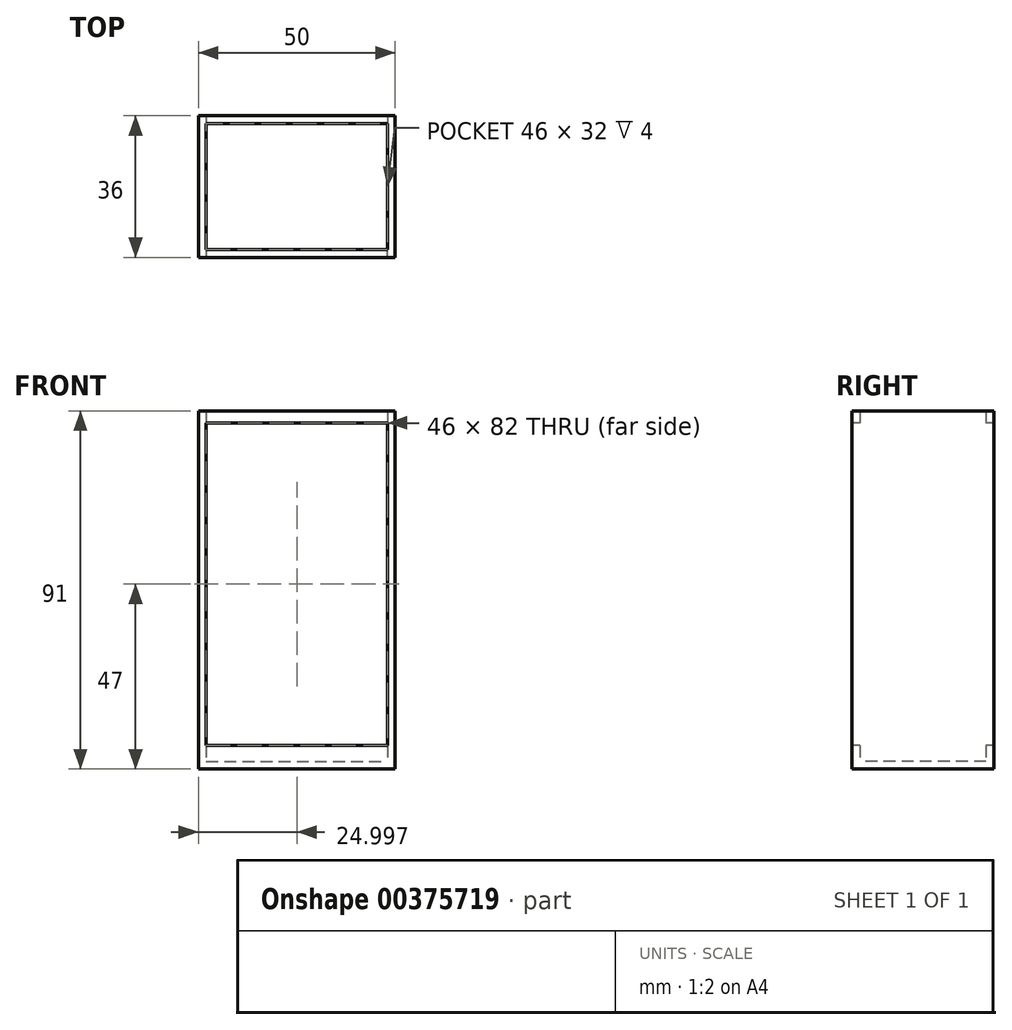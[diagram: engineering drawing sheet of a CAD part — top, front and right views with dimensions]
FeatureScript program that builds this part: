
annotation { "Feature Type Name" : "Feature", "Feature Type Description" : "" }
export const myFeature = defineFeature(function(context is Context, id is Id, definition is map)
    precondition{}
    {
        {
            var Q0;
            Q0=qCreatedBy(makeId("Top.planeOp"),FACE);
            var sketch = newSketch(context, id + "F0", { "sketchPlane" : qUnion([Q0])});
            skLineSegment(sketch, "E0.bottom", {"start": v(-57.9, 42.38) * mm, "end": v(-7.9, 42.38) * mm});
            skLineSegment(sketch, "E0.top", {"start": v(-57.9, 6.38) * mm, "end": v(-7.9, 6.38) * mm});
            skLineSegment(sketch, "E0.left", {"start": v(-57.9, 42.38) * mm, "end": v(-57.9, 6.38) * mm});
            skLineSegment(sketch, "E0.right", {"start": v(-7.9, 42.38) * mm, "end": v(-7.9, 6.38) * mm});
            skSolve(sketch);
        }
        {
            var Q0;
            Q0 = qSketchRegion(id + "F0", true);
            extrude(context, id + "F1", {"entities" : qUnion([Q0]), "depth" : 2 * mm});
        }
        {
            var Q0;
            Q0=makeQuery(id+"F1.opExtrude","CAP_FACE",FACE,{"disambiguationData":[OSD([sQuery(id+"F0.wireOp",EDGE,"E0.bottom"),sQuery(id+"F0.wireOp",EDGE,"E0.top"),sQuery(id+"F0.wireOp",EDGE,"E0.left"),sQuery(id+"F0.wireOp",EDGE,"E0.right")])],"isStart":false});
            var sketch = newSketch(context, id + "F2", { "sketchPlane" : qUnion([Q0])});
            skLineSegment(sketch, "E1.bottom", {"start": v(-57.9, 42.38) * mm, "end": v(-7.9, 42.38) * mm});
            skLineSegment(sketch, "E1.top", {"start": v(-57.9, 6.38) * mm, "end": v(-7.9, 6.38) * mm});
            skLineSegment(sketch, "E1.left", {"start": v(-57.9, 42.38) * mm, "end": v(-57.9, 6.38) * mm});
            skLineSegment(sketch, "E1.right", {"start": v(-7.9, 42.38) * mm, "end": v(-7.9, 6.38) * mm});
            skLineSegment(sketch, "E2.bottom", {"start": v(-55.9, 40.38) * mm, "end": v(-9.9, 40.38) * mm});
            skLineSegment(sketch, "E2.top", {"start": v(-55.9, 8.38) * mm, "end": v(-9.9, 8.38) * mm});
            skLineSegment(sketch, "E2.left", {"start": v(-55.9, 40.38) * mm, "end": v(-55.9, 8.38) * mm});
            skLineSegment(sketch, "E2.right", {"start": v(-9.9, 40.38) * mm, "end": v(-9.9, 8.38) * mm});
            skSolve(sketch);
        }
        {
            var Q0;
            Q0 = qSketchRegion(id + "F2", true);
            extrude(context, id + "F3", {"entities" : qUnion([Q0]), "operationType" : NewBodyOperationType.ADD, "depth" : 4 * mm});
        }
        {
            var Q0;
            Q0=makeQuery(id+"F3.opExtrude","CAP_FACE",FACE,{"disambiguationData":[OSD([sQuery(id+"F2.wireOp",EDGE,"E1.bottom"),sQuery(id+"F2.wireOp",EDGE,"E1.top"),sQuery(id+"F2.wireOp",EDGE,"E1.left"),sQuery(id+"F2.wireOp",EDGE,"E1.right"),sQuery(id+"F2.wireOp",EDGE,"E2.bottom"),sQuery(id+"F2.wireOp",EDGE,"E2.top"),sQuery(id+"F2.wireOp",EDGE,"E2.left"),sQuery(id+"F2.wireOp",EDGE,"E2.right")])],"isStart":false});
            var sketch = newSketch(context, id + "F4", { "sketchPlane" : qUnion([Q0])});
            skLineSegment(sketch, "E3.bottom", {"start": v(-57.9, 6.38) * mm, "end": v(-55.9, 6.38) * mm});
            skLineSegment(sketch, "E3.top", {"start": v(-57.9, 42.38) * mm, "end": v(-55.9, 42.38) * mm});
            skLineSegment(sketch, "E3.left", {"start": v(-57.9, 6.38) * mm, "end": v(-57.9, 42.38) * mm});
            skLineSegment(sketch, "E3.right", {"start": v(-55.9, 6.38) * mm, "end": v(-55.9, 42.38) * mm});
            skLineSegment(sketch, "E4.bottom", {"start": v(-9.9, 6.38) * mm, "end": v(-7.9, 6.38) * mm});
            skLineSegment(sketch, "E4.top", {"start": v(-9.9, 42.38) * mm, "end": v(-7.9, 42.38) * mm});
            skLineSegment(sketch, "E4.left", {"start": v(-9.9, 6.38) * mm, "end": v(-9.9, 42.38) * mm});
            skLineSegment(sketch, "E4.right", {"start": v(-7.9, 6.38) * mm, "end": v(-7.9, 42.38) * mm});
            skSolve(sketch);
        }
        {
            var Q0;
            Q0 = qSketchRegion(id + "F4", true);
            extrude(context, id + "F5", {"entities" : qUnion([Q0]), "operationType" : NewBodyOperationType.ADD, "depth" : 85 * mm});
        }
        {
            var Q0;
            Q0=makeQuery(id+"F5.opExtrude","CAP_FACE",FACE,{"disambiguationData":[OSD([sQuery(id+"F4.wireOp",EDGE,"E3.bottom"),sQuery(id+"F4.wireOp",EDGE,"E3.top"),sQuery(id+"F4.wireOp",EDGE,"E3.left"),sQuery(id+"F4.wireOp",EDGE,"E3.right")])],"isStart":false});
            var sketch = newSketch(context, id + "F6", { "sketchPlane" : qUnion([Q0])});
            skLineSegment(sketch, "E5.bottom", {"start": v(-57.9, 42.38) * mm, "end": v(-7.9, 42.38) * mm});
            skLineSegment(sketch, "E5.top", {"start": v(-57.9, 6.38) * mm, "end": v(-7.9, 6.38) * mm});
            skLineSegment(sketch, "E5.left", {"start": v(-57.9, 42.38) * mm, "end": v(-57.9, 6.38) * mm});
            skLineSegment(sketch, "E5.right", {"start": v(-7.9, 42.38) * mm, "end": v(-7.9, 6.38) * mm});
            skSolve(sketch);
        }
        {
            var Q0;
            Q0 = qSketchRegion(id + "F6", true);
            extrude(context, id + "F7", {"entities" : qUnion([Q0]), "operationType" : NewBodyOperationType.ADD, "oppositeDirection" : true, "depth" : 3 * mm});
        }
        {
            var Q0;
            Q0=makeQuery(id+"F7.opExtrude","CAP_FACE",FACE,{"disambiguationData":[OSD([sQuery(id+"F6.wireOp",EDGE,"E5.bottom"),sQuery(id+"F6.wireOp",EDGE,"E5.top"),sQuery(id+"F6.wireOp",EDGE,"E5.left"),sQuery(id+"F6.wireOp",EDGE,"E5.right")])],"isStart":false});
            var sketch = newSketch(context, id + "F8", { "sketchPlane" : qUnion([Q0])});
            skLineSegment(sketch, "E6.bottom", {"start": v(-55.9, -8.38) * mm, "end": v(-9.9, -8.38) * mm});
            skLineSegment(sketch, "E6.top", {"start": v(-55.9, -40.38) * mm, "end": v(-9.9, -40.38) * mm});
            skLineSegment(sketch, "E6.left", {"start": v(-55.9, -8.38) * mm, "end": v(-55.9, -40.38) * mm});
            skLineSegment(sketch, "E6.right", {"start": v(-9.9, -8.38) * mm, "end": v(-9.9, -40.38) * mm});
            skSolve(sketch);
        }
        {
            var Q0;
            Q0 = qSketchRegion(id + "F8", true);
            extrude(context, id + "F9", {"entities" : qUnion([Q0]), "operationType" : NewBodyOperationType.REMOVE, "oppositeDirection" : true, "depth" : 25 * mm});
        }
    });
